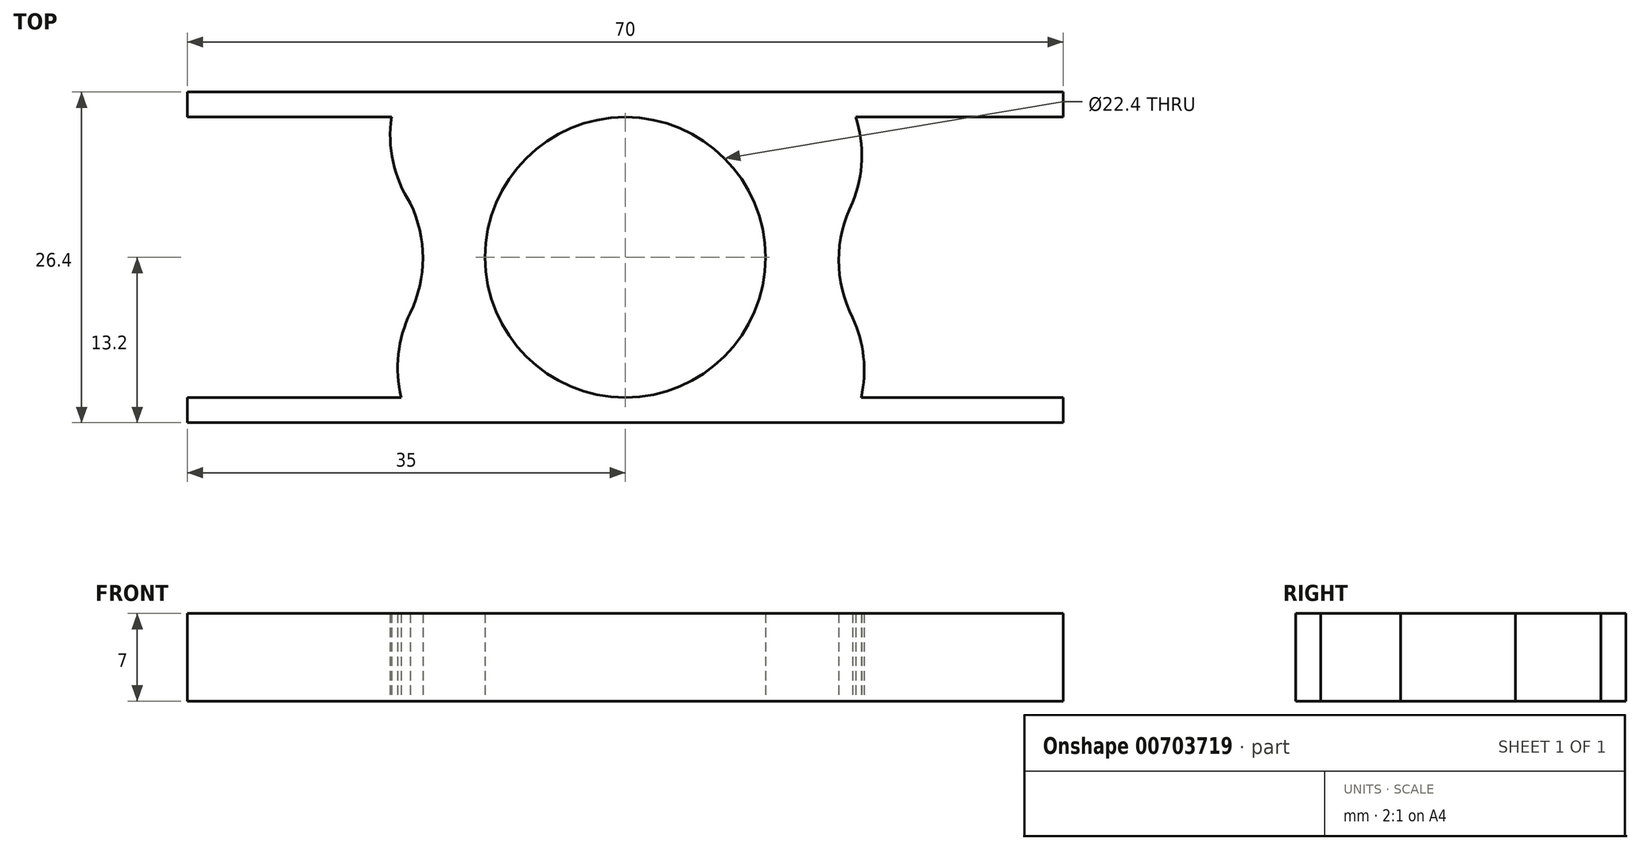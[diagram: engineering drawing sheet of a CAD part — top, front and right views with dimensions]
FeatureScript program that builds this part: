
annotation { "Feature Type Name" : "Feature", "Feature Type Description" : "" }
export const myFeature = defineFeature(function(context is Context, id is Id, definition is map)
    precondition{}
    {
        {
            var Q0;
            Q0=qCreatedBy(makeId("Top.planeOp"),FACE);
            var sketch = newSketch(context, id + "F0", { "sketchPlane" : qUnion([Q0])});
            skPoint(sketch, "E0.start.orphan", {"position": v(-35, -10.23) * mm});
            skCircle(sketch, "E1", {"center": v(0, 0) * mm, "radius": 11.2 * mm});
            skArc(sketch, "E2", {"start": v(-18.68, 11.2) * mm, "mid": v(-18.55, 7.62) * mm, "end": v(-17.17, 4.31) * mm});
            skArc(sketch, "E3", {"start": v(-17.17, -4.43) * mm, "mid": v(-16.17, -0.06) * mm, "end": v(-17.17, 4.31) * mm});
            skArc(sketch, "E4", {"start": v(-17.17, -4.43) * mm, "mid": v(-18.13, -7.75) * mm, "end": v(-17.9, -11.2) * mm});
            skLineSegment(sketch, "E5", {"start": v(-16.17, 0) * mm, "end": v(-11.2, 0) * mm, "construction": true});
            skLineSegment(sketch, "E6", {"start": v(13.2, 0) * mm, "end": v(18.17, 0) * mm, "construction": true});
            skArc(sketch, "E7", {"start": v(18.17, 4.38) * mm, "mid": v(18.89, 7.77) * mm, "end": v(18.4, 11.2) * mm});
            skArc(sketch, "E8", {"start": v(18.17, 4.38) * mm, "mid": v(17.05, -0.22) * mm, "end": v(18.17, -4.82) * mm});
            skArc(sketch, "E9", {"start": v(18.84, -11.2) * mm, "mid": v(19.03, -7.96) * mm, "end": v(18.17, -4.82) * mm});
            skPoint(sketch, "E10.orphan", {"position": v(0, 13.2) * mm});
            skPoint(sketch, "E11.orphan", {"position": v(0, -13.2) * mm});
            skPoint(sketch, "E12.end.orphan", {"position": v(35, 13.2) * mm});
            skPoint(sketch, "E13.start.orphan", {"position": v(-35, -13.2) * mm});
            skLineSegment(sketch, "E14", {"start": v(17.5, 13.2) * mm, "end": v(35, 13.2) * mm});
            skLineSegment(sketch, "E15", {"start": v(18.17, -13.2) * mm, "end": v(35, -13.2) * mm});
            skLineSegment(sketch, "E16", {"start": v(-17.17, -13.2) * mm, "end": v(-35, -13.2) * mm});
            skLineSegment(sketch, "E17", {"start": v(-35, 13.2) * mm, "end": v(-18.17, 13.2) * mm});
            skPoint(sketch, "E18.start.orphan", {"position": v(-35, 16.2) * mm});
            skPoint(sketch, "E19.end.orphan", {"position": v(17.5, 16.2) * mm});
            skPoint(sketch, "E20.end.orphan", {"position": v(35, 16.2) * mm});
            skPoint(sketch, "E21.end.orphan", {"position": v(18.17, -16.2) * mm});
            skPoint(sketch, "E22.end.orphan", {"position": v(35, -16.2) * mm});
            skPoint(sketch, "E23.start.orphan", {"position": v(-35, -16.2) * mm});
            skLineSegment(sketch, "E24", {"start": v(-17.17, -13.2) * mm, "end": v(18.17, -13.2) * mm});
            skLineSegment(sketch, "E25", {"start": v(-18.17, 13.2) * mm, "end": v(17.5, 13.2) * mm});
            skLineSegment(sketch, "E26", {"start": v(19.02, -10.2) * mm, "end": v(18.17, -10.2) * mm});
            skLineSegment(sketch, "E27", {"start": v(35, 13.2) * mm, "end": v(35, 11.2) * mm});
            skLineSegment(sketch, "E28", {"start": v(35, 11.2) * mm, "end": v(18.4, 11.2) * mm});
            skLineSegment(sketch, "E29", {"start": v(-35, 13.2) * mm, "end": v(-35, 11.2) * mm});
            skLineSegment(sketch, "E30", {"start": v(-18.68, 11.2) * mm, "end": v(-18.17, 11.2) * mm});
            skLineSegment(sketch, "E31", {"start": v(-35, 11.2) * mm, "end": v(-18.17, 11.2) * mm});
            skLineSegment(sketch, "E32", {"start": v(35, -13.2) * mm, "end": v(35, -11.2) * mm});
            skLineSegment(sketch, "E33", {"start": v(-35, -13.2) * mm, "end": v(-35, -11.2) * mm});
            skLineSegment(sketch, "E34", {"start": v(-35, -11.2) * mm, "end": v(-17.9, -11.2) * mm});
            skLineSegment(sketch, "E35", {"start": v(35, -11.2) * mm, "end": v(35, -13.2) * mm});
            skLineSegment(sketch, "E36", {"start": v(35, -13.2) * mm, "end": v(18.17, -13.2) * mm});
            skPoint(sketch, "E37.end.orphan", {"position": v(19.02, -11.2) * mm});
            skLineSegment(sketch, "E38", {"start": v(35, -11.2) * mm, "end": v(18.17, -11.2) * mm});
            skSolve(sketch);
        }
        {
            var Q0;
            Q0=makeQuery(id+"F0.imprint","IMPRINT",FACE,{"disambiguationData":[TD([[makeQuery(id+"F0.imprint","IMPRINT",EDGE,{"derivedFrom":sQuery(id+"F0.wireOp",EDGE,"E1")}),-1.0]])]});
            var Q1;
            {var subQ0=sQuery(id+"F0.wireOp",EDGE,"E14");Q1=makeQuery(id+"F0.imprint","IMPRINT",FACE,{"disambiguationData":[TD([[makeQuery(id+"F0.imprint","IMPRINT",EDGE,{"derivedFrom":subQ0}),-1.0]])]});}
            var Q2;
            {var subQ4=sQuery(id+"F0.wireOp",EDGE,"E35");Q2=makeQuery(id+"F0.imprint","IMPRINT",FACE,{"disambiguationData":[TD([[makeQuery(id+"F0.imprint","IMPRINT",EDGE,{"derivedFrom":subQ4}),-1.0]])]});}
            var Q3;
            {var subQ0=sQuery(id+"F0.wireOp",EDGE,"E17");Q3=makeQuery(id+"F0.imprint","IMPRINT",FACE,{"disambiguationData":[TD([[makeQuery(id+"F0.imprint","IMPRINT",EDGE,{"derivedFrom":subQ0}),-1.0]])]});}
            var Q4;
            {var subQ0=sQuery(id+"F0.wireOp",EDGE,"E16");Q4=makeQuery(id+"F0.imprint","IMPRINT",FACE,{"disambiguationData":[TD([[makeQuery(id+"F0.imprint","IMPRINT",EDGE,{"derivedFrom":subQ0}),-1.0]])]});}
            extrude(context, id + "F1", {"entities" : qUnion([Q0, Q1, Q2, Q3, Q4]), "depth" : 7 * mm, "offsetDistance" : 25 * mm});
        }
    });
